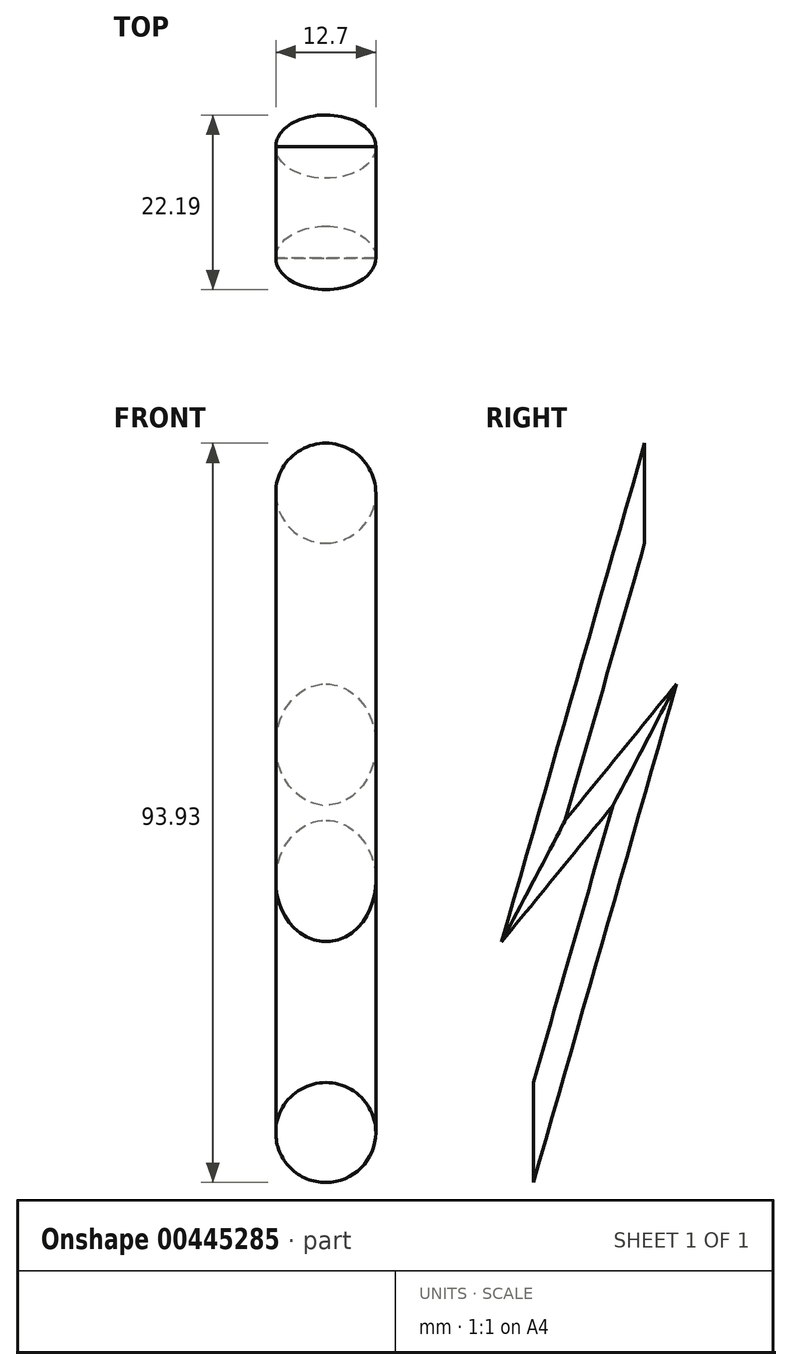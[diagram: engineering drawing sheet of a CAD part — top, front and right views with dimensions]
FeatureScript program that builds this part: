
annotation { "Feature Type Name" : "Feature", "Feature Type Description" : "" }
export const myFeature = defineFeature(function(context is Context, id is Id, definition is map)
    precondition{}
    {
        {
            var Q0;
            Q0=qCreatedBy(makeId("Front.planeOp"),FACE);
            var sketch = newSketch(context, id + "F0", { "sketchPlane" : qUnion([Q0])});
            skPoint(sketch, "E0.middle", {"position": v(0, 0) * mm});
            skCircle(sketch, "E1", {"center": v(0, 0) * mm, "radius": 6.35 * mm});
            skSolve(sketch);
        }
        {
            var Q0;
            Q0=qCreatedBy(makeId("Right.planeOp"),FACE);
            var sketch = newSketch(context, id + "F1", { "sketchPlane" : qUnion([Q0])});
            skLineSegment(sketch, "E2", {"start": v(0, 0) * mm, "end": v(14.13, 49.28) * mm});
            skLineSegment(sketch, "E3", {"start": v(14.13, 49.28) * mm, "end": v(0, 31.95) * mm});
            skLineSegment(sketch, "E4", {"start": v(0, 31.95) * mm, "end": v(14.13, 81.23) * mm});
            skSolve(sketch);
        }
        {
            var Q0;
            Q0=makeQuery(id+"F0.imprint","IMPRINT",FACE,{"disambiguationData":[TD([[makeQuery(id+"F0.imprint","IMPRINT",EDGE,{"derivedFrom":sQuery(id+"F0.wireOp",EDGE,"E1")}),1.0]])]});
            var Q1;
            Q1=sQuery(id+"F1.wireOp",EDGE,"E4");
            var Q2;
            Q2=sQuery(id+"F1.wireOp",EDGE,"E3");
            var Q3;
            Q3=sQuery(id+"F1.wireOp",EDGE,"E2");
            sweep(context, id + "F2", {"profiles" : qUnion([Q0]), "path" : qUnion([Q1, Q2, Q3])});
        }
    });
